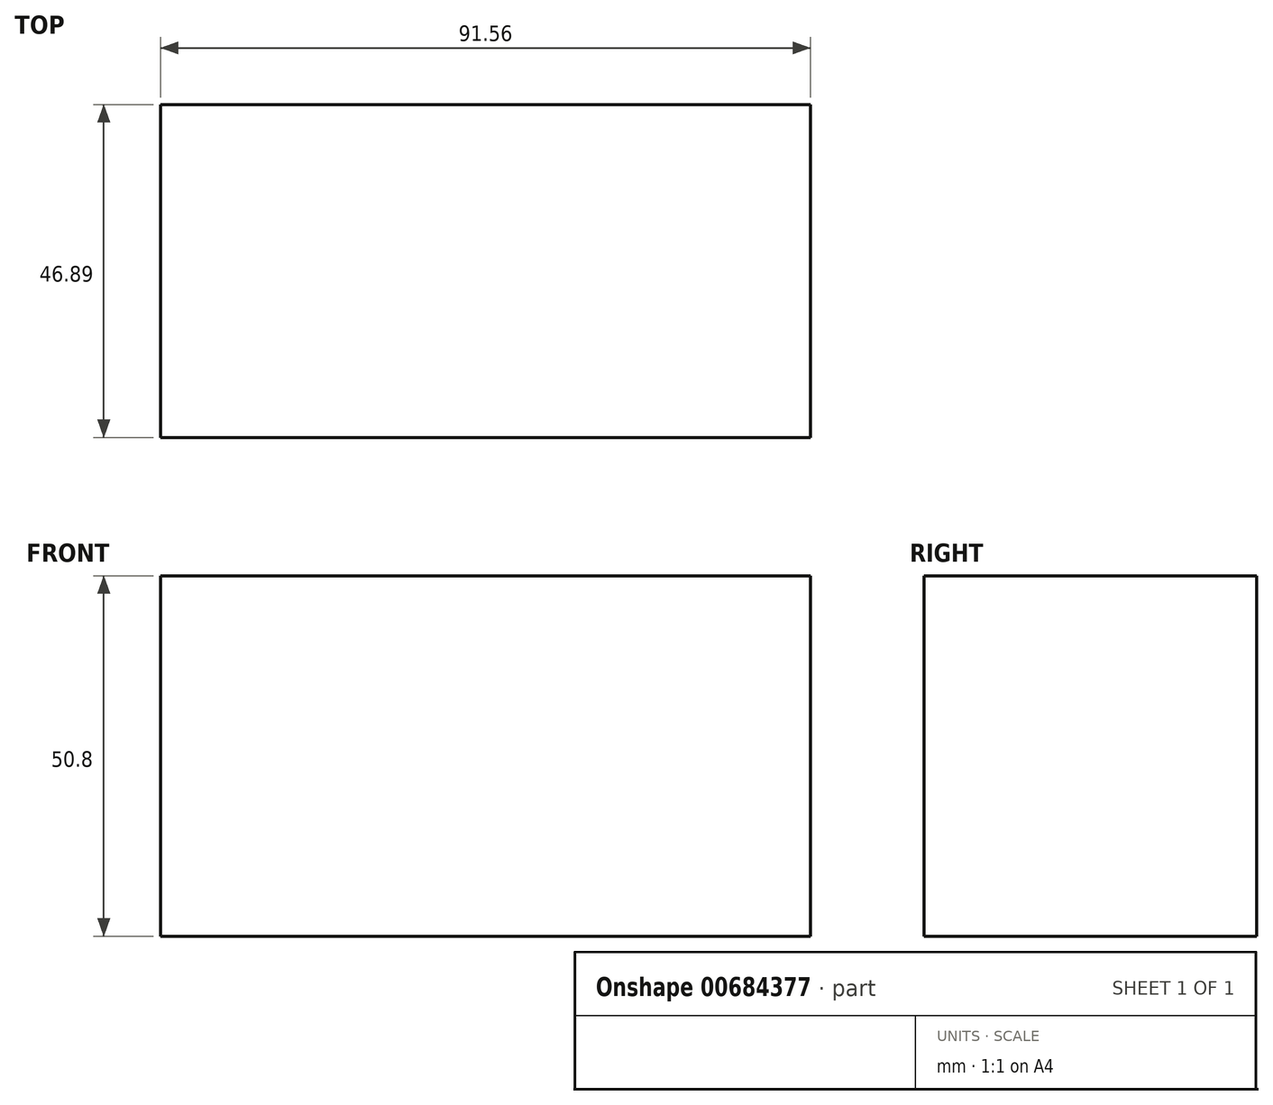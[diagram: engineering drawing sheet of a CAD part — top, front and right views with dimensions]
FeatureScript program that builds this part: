
annotation { "Feature Type Name" : "Feature", "Feature Type Description" : "" }
export const myFeature = defineFeature(function(context is Context, id is Id, definition is map)
    precondition{}
    {
        {
            var Q0;
            Q0=qCreatedBy(makeId("Top.planeOp"),FACE);
            var sketch = newSketch(context, id + "F0", { "sketchPlane" : qUnion([Q0])});
            skLineSegment(sketch, "E0.bottom", {"start": v(0, 0) * mm, "end": v(-91.56, 0) * mm});
            skLineSegment(sketch, "E0.top", {"start": v(0, 46.9) * mm, "end": v(-91.56, 46.9) * mm});
            skLineSegment(sketch, "E0.left", {"start": v(0, 0) * mm, "end": v(0, 46.9) * mm});
            skLineSegment(sketch, "E0.right", {"start": v(-91.56, 0) * mm, "end": v(-91.56, 46.9) * mm});
            skSolve(sketch);
        }
        {
            var Q0;
            Q0=makeQuery(id+"F0.imprint","IMPRINT",FACE,{"disambiguationData":[TD([[makeQuery(id+"F0.imprint","IMPRINT",EDGE,{"derivedFrom":sQuery(id+"F0.wireOp",EDGE,"E0.bottom")}),-1.0]])]});
            var sketch = newSketch(context, id + "F1", { "sketchPlane" : qUnion([Q0])});
            skSolve(sketch);
        }
        {
            var Q0;
            Q0=makeQuery(id+"F1.imprint","IMPRINT",FACE,{"disambiguationData":[TD([[makeQuery(id+"F1.imprint","IMPRINT",EDGE,{"derivedFrom":makeQuery(id+"F0.imprint","IMPRINT",EDGE,{"derivedFrom":sQuery(id+"F0.wireOp",EDGE,"E0.bottom")})}),-1.0]])]});
            extrude(context, id + "F2", {"entities" : qUnion([Q0]), "depth" : 50.8 * mm, "offsetDistance" : 25.4 * mm});
        }
    });
